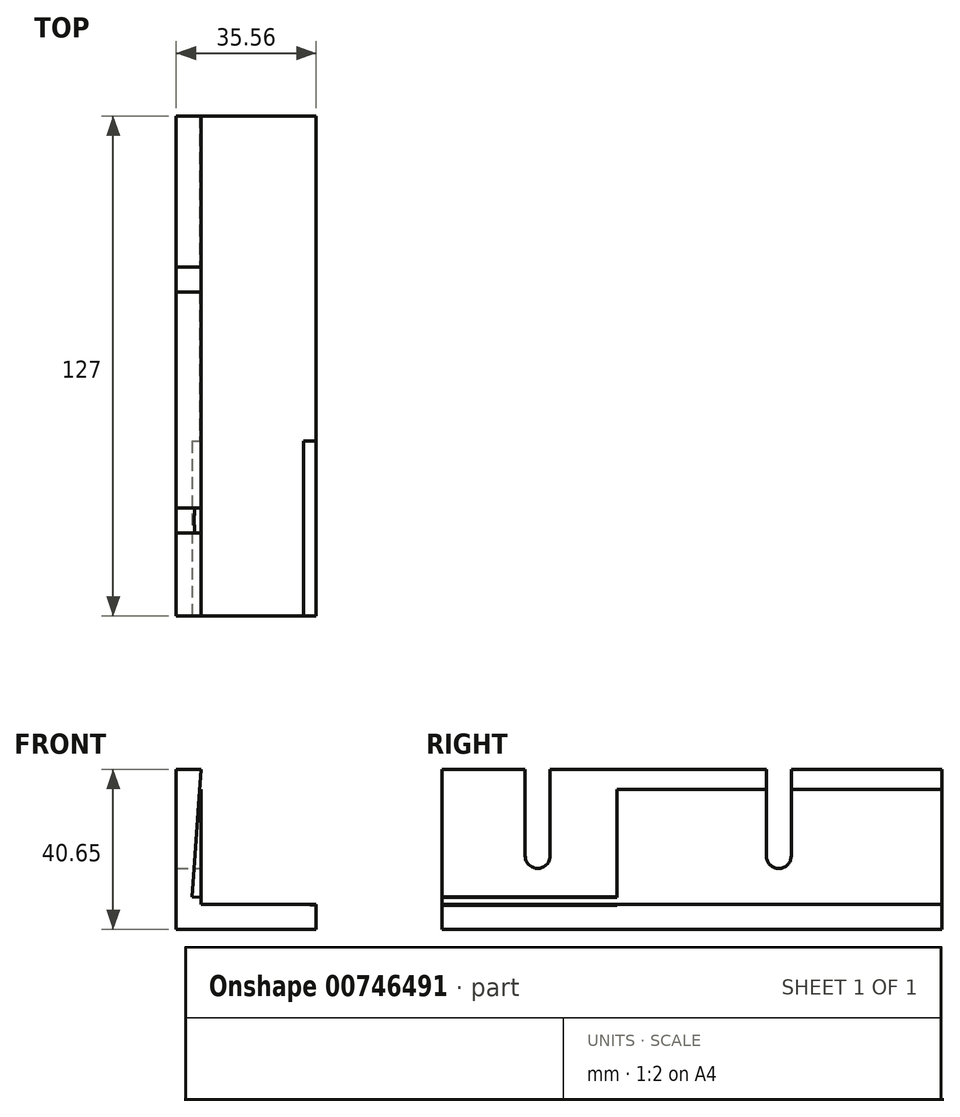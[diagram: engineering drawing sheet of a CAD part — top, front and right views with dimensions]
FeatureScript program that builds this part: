
annotation { "Feature Type Name" : "Feature", "Feature Type Description" : "" }
export const myFeature = defineFeature(function(context is Context, id is Id, definition is map)
    precondition{}
    {
        {
            var Q0;
            Q0=qCreatedBy(makeId("Front.planeOp"),FACE);
            var sketch = newSketch(context, id + "F0", { "sketchPlane" : qUnion([Q0])});
            skLineSegment(sketch, "E0", {"start": v(-33.64, 24.98) * mm, "end": v(-33.64, -39.73) * mm});
            skLineSegment(sketch, "E1", {"start": v(-33.64, -39.73) * mm, "end": v(31.06, -39.73) * mm});
            skLineSegment(sketch, "E2", {"start": v(31.06, -39.73) * mm, "end": v(31.06, 24.98) * mm});
            skLineSegment(sketch, "E3", {"start": v(-33.64, 24.98) * mm, "end": v(31.06, 24.98) * mm});
            skSolve(sketch);
        }
        {
            var Q0;
            Q0=makeQuery(id+"F0.imprint","IMPRINT",FACE,{"disambiguationData":[TD([[makeQuery(id+"F0.imprint","IMPRINT",EDGE,{"derivedFrom":sQuery(id+"F0.wireOp",EDGE,"E0")}),1.0]])]});
            extrude(context, id + "F1", {"entities" : qUnion([Q0]), "oppositeDirection" : true, "depth" : 127 * mm, "offsetDistance" : 25.4 * mm});
        }
        {
            var Q0;
            Q0=makeQuery(id+"F1.opExtrude","CAP_FACE",FACE,{"disambiguationData":[OSD([sQuery(id+"F0.wireOp",EDGE,"E0"),sQuery(id+"F0.wireOp",EDGE,"E1"),sQuery(id+"F0.wireOp",EDGE,"E2"),sQuery(id+"F0.wireOp",EDGE,"E3")])],"isStart":false});
            var sketch = newSketch(context, id + "F2", { "sketchPlane" : qUnion([Q0])});
            skLineSegment(sketch, "E4", {"start": v(33.64, -39.73) * mm, "end": v(33.64, -33.38) * mm});
            skLineSegment(sketch, "E5", {"start": v(33.64, -33.38) * mm, "end": v(27.3, -33.38) * mm});
            skLineSegment(sketch, "E6", {"start": v(27.3, -33.38) * mm, "end": v(27.3, -39.73) * mm});
            skLineSegment(sketch, "E7", {"start": v(27.3, -33.38) * mm, "end": v(-31.06, -33.38) * mm});
            skLineSegment(sketch, "E8", {"start": v(27.3, -33.38) * mm, "end": v(27.3, 24.98) * mm});
            skSolve(sketch);
        }
        {
            var Q0;
            {var subQ0=sQuery(id+"F2.wireOp",EDGE,"E7");Q0=makeQuery(id+"F2.imprint","IMPRINT",FACE,{"disambiguationData":[TD([[makeQuery(id+"F2.imprint","IMPRINT",EDGE,{"derivedFrom":subQ0}),-1.0]])]});}
            extrude(context, id + "F3", {"entities" : qUnion([Q0]), "operationType" : NewBodyOperationType.REMOVE, "endBound" : BoundingType.THROUGH_ALL, "oppositeDirection" : true, "depth" : 55.76 * mm, "offsetDistance" : 25.4 * mm});
        }
        {
            var Q0;
            Q0=makeQuery(id+"F1.opExtrude","CAP_FACE",FACE,{"disambiguationData":[OSD([sQuery(id+"F0.wireOp",EDGE,"E0"),sQuery(id+"F0.wireOp",EDGE,"E1"),sQuery(id+"F0.wireOp",EDGE,"E2"),sQuery(id+"F0.wireOp",EDGE,"E3")])],"isStart":true});
            var sketch = newSketch(context, id + "F4", { "sketchPlane" : qUnion([Q0])});
            skLineSegment(sketch, "E9", {"start": v(-27.3, 24.98) * mm, "end": v(-33.64, 24.98) * mm});
            skLineSegment(sketch, "E10", {"start": v(-33.64, 24.98) * mm, "end": v(-33.64, -39.73) * mm});
            skLineSegment(sketch, "E11", {"start": v(-33.64, -39.73) * mm, "end": v(31.06, -39.73) * mm});
            skPoint(sketch, "E12.endSnap0", {"position": v(31.06, -36.55) * mm});
            skLineSegment(sketch, "E13", {"start": v(-29.55, -31.4) * mm, "end": v(53, -37.17) * mm});
            skLineSegment(sketch, "E14", {"start": v(-29.55, -31.4) * mm, "end": v(-25.06, 32.88) * mm});
            skLineSegment(sketch, "E15", {"start": v(53, -37.17) * mm, "end": v(53, -39.73) * mm});
            skLineSegment(sketch, "E16", {"start": v(53, -39.73) * mm, "end": v(-33.64, -39.73) * mm});
            skLineSegment(sketch, "E17", {"start": v(-33.64, 32.88) * mm, "end": v(-25.06, 32.88) * mm});
            skLineSegment(sketch, "E18", {"start": v(-33.64, 32.88) * mm, "end": v(-33.64, -39.73) * mm});
            skSolve(sketch);
        }
        {
            var Q0;
            {var subQ0=sQuery(id+"F4.wireOp",EDGE,"E14");var subQ1=sQuery(id+"F4.wireOp",EDGE,"E13");var subQ2=makeQuery(id+"F4.imprint","INTERSECT",VERTEX,{"derivedFrom":[subQ1,subQ0]});Q0=makeQuery(id+"F4.imprint","IMPRINT",FACE,{"disambiguationData":[TD([[makeQuery(id+"F4.imprint","IMPRINT",EDGE,{"disambiguationData":[TD([[subQ2,-1.0]])],"derivedFrom":subQ1}),1.0]])]});}
            var Q1;
            {var subQ0=sQuery(id+"F4.wireOp",EDGE,"E13");var subQ1=sQuery(id+"F0.wireOp",EDGE,"E2");var subQ4=makeQuery(id+"F1.opExtrude","CAP_EDGE",EDGE,{"disambiguationData":[OSD([subQ1])],"isStart":true});var subQ5=makeQuery(id+"F4.imprint","INTERSECT",VERTEX,{"derivedFrom":[subQ4,subQ0]});Q1=makeQuery(id+"F4.imprint","IMPRINT",FACE,{"disambiguationData":[TD([[makeQuery(id+"F4.imprint","IMPRINT",EDGE,{"disambiguationData":[TD([[subQ5,1.0]])],"derivedFrom":subQ0}),1.0]])]});}
            extrude(context, id + "F5", {"entities" : qUnion([Q0, Q1]), "operationType" : NewBodyOperationType.REMOVE, "oppositeDirection" : true, "depth" : 44.45 * mm, "offsetDistance" : 25.4 * mm});
        }
        {
            var Q0;
            Q0=makeQuery(id+"F3.boolean.opBoolean","COPY",FACE,{"derivedFrom":makeQuery(id+"F3.opExtrude","SWEPT_FACE",FACE,{"disambiguationData":[OSD([sQuery(id+"F2.wireOp",EDGE,"E8")])]})});
            var sketch = newSketch(context, id + "F6", { "sketchPlane" : qUnion([Q0])});
            skLineSegment(sketch, "E19", {"start": v(27.44, 24.98) * mm, "end": v(127, 24.98) * mm});
            skLineSegment(sketch, "E20", {"start": v(127, 24.98) * mm, "end": v(127, -33.38) * mm});
            skLineSegment(sketch, "E21", {"start": v(127, -33.38) * mm, "end": v(0, -33.38) * mm});
            skLineSegment(sketch, "E22", {"start": v(0, -33.38) * mm, "end": v(0, 24.98) * mm});
            skLineSegment(sketch, "E23", {"start": v(0, 24.98) * mm, "end": v(21.09, 24.98) * mm});
            skArc(sketch, "E24", {"start": v(82.35, -21.06) * mm, "mid": v(85.53, -24.23) * mm, "end": v(88.7, -21.06) * mm});
            skLineSegment(sketch, "E25", {"start": v(88.7, -21.06) * mm, "end": v(88.7, 24.98) * mm});
            skLineSegment(sketch, "E26", {"start": v(82.35, -21.06) * mm, "end": v(82.35, 24.98) * mm});
            skArc(sketch, "E27", {"start": v(21.09, -21.06) * mm, "mid": v(24.26, -24.23) * mm, "end": v(27.44, -21.06) * mm});
            skLineSegment(sketch, "E28", {"start": v(21.09, -21.06) * mm, "end": v(21.09, 24.98) * mm});
            skLineSegment(sketch, "E29", {"start": v(27.44, -21.06) * mm, "end": v(27.44, 24.98) * mm});
            skLineSegment(sketch, "E30", {"start": v(27.44, 24.98) * mm, "end": v(21.09, 24.98) * mm});
            skPoint(sketch, "E31.endSnap0", {"position": v(24.26, -24.23) * mm});
            skSolve(sketch);
        }
        {
            var Q0;
            {var subQ1=sQuery(id+"F6.wireOp",EDGE,"c31WWHYK-vBc0-QJFG-3EGz-c6wR2XxRCZ5n");var subQ4=sQuery(id+"F6.wireOp",EDGE,"BnuWwshu-QowS-UM11-6egq-2gLvmHulIOIC");var subQ5=makeQuery(id+"F6.imprint","INTERSECT",VERTEX,{"derivedFrom":[subQ1,subQ4]});Q0=makeQuery(id+"F6.imprint","IMPRINT",FACE,{"disambiguationData":[TD([[makeQuery(id+"F6.imprint","IMPRINT",EDGE,{"disambiguationData":[TD([[subQ5,-1.0]])],"derivedFrom":subQ1}),1.0]])]});}
            var Q1;
            {var subQ0=sQuery(id+"F6.wireOp",EDGE,"PxgFI6bS-cj6o-HxTh-fpXl-rELYx5VuJGPC");var subQ9=sQuery(id+"F6.wireOp",EDGE,"BnuWwshu-QowS-UM11-6egq-2gLvmHulIOIC");var subQ10=makeQuery(id+"F6.imprint","INTERSECT",VERTEX,{"derivedFrom":[subQ0,subQ9]});Q1=makeQuery(id+"F6.imprint","IMPRINT",FACE,{"disambiguationData":[TD([[makeQuery(id+"F6.imprint","IMPRINT",EDGE,{"disambiguationData":[TD([[subQ10,-1.0]])],"derivedFrom":subQ0}),-1.0]])]});}
            var Q2;
            Q2=makeQuery(id+"F6.imprint","IMPRINT",FACE,{"disambiguationData":[TD([[makeQuery(id+"F6.imprint","IMPRINT",EDGE,{"derivedFrom":sQuery(id+"F6.wireOp",EDGE,"nVCfulUX-UBZk-rReu-1cFz-JZFjZ0D3dsWO")}),1.0]])]});
            var Q3;
            {var subQ0=sQuery(id+"F6.wireOp",EDGE,"BnuWwshu-QowS-UM11-6egq-2gLvmHulIOIC");var subQ1=sQuery(id+"F2.wireOp",EDGE,"E8");var subQ2=sQuery(id+"F0.wireOp",EDGE,"E3");var subQ3=makeQuery(id+"F3.boolean.opBoolean","COPY",EDGE,{"derivedFrom":makeQuery(id+"F3.opExtrude","SWEPT_EDGE",EDGE,{"disambiguationData":[OSD([subQ2,subQ1])]})});var subQ4=makeQuery(id+"F6.imprint","INTERSECT",VERTEX,{"derivedFrom":[subQ3,subQ0]});Q3=makeQuery(id+"F6.imprint","IMPRINT",FACE,{"disambiguationData":[TD([[makeQuery(id+"F6.imprint","IMPRINT",EDGE,{"disambiguationData":[TD([[subQ4,-1.0]])],"derivedFrom":subQ3}),-1.0]])]});}
            var Q4;
            {var subQ0=sQuery(id+"F6.wireOp",EDGE,"E23");var subQ1=sQuery(id+"F6.wireOp",EDGE,"GWAlOemz-n7tp-SVu9-tSwS-dO0S4uVOhK2H");var subQ2=makeQuery(id+"F6.imprint","INTERSECT",VERTEX,{"derivedFrom":[subQ1,subQ0]});Q4=makeQuery(id+"F6.imprint","IMPRINT",FACE,{"disambiguationData":[TD([[makeQuery(id+"F6.imprint","IMPRINT",EDGE,{"disambiguationData":[TD([[subQ2,-1.0]])],"derivedFrom":subQ0}),-1.0]])]});}
            var Q5;
            {var subQ0=sQuery(id+"F6.wireOp",EDGE,"YNUtTdzb-W802-iu6F-8lba-iVoMnU8XWFkd");Q5=makeQuery(id+"F6.imprint","IMPRINT",FACE,{"disambiguationData":[TD([[makeQuery(id+"F6.imprint","IMPRINT",EDGE,{"derivedFrom":subQ0}),1.0]])]});}
            var Q6;
            Q6=makeQuery(id+"F6.imprint","IMPRINT",FACE,{"disambiguationData":[TD([[makeQuery(id+"F6.imprint","IMPRINT",EDGE,{"derivedFrom":sQuery(id+"F6.wireOp",EDGE,"f8IW44Pr-O293-7rfo-ai8i-kcAhvm2oJwU2")}),1.0]])]});
            var Q7;
            {var subQ0=sQuery(id+"F6.wireOp",EDGE,"E30");Q7=makeQuery(id+"F6.imprint","IMPRINT",FACE,{"disambiguationData":[TD([[makeQuery(id+"F6.imprint","IMPRINT",EDGE,{"derivedFrom":subQ0}),-1.0]])]});}
            var Q8;
            {var subQ0=sQuery(id+"F6.wireOp",EDGE,"E27");Q8=makeQuery(id+"F6.imprint","IMPRINT",FACE,{"disambiguationData":[TD([[makeQuery(id+"F6.imprint","IMPRINT",EDGE,{"derivedFrom":subQ0}),1.0]])]});}
            var Q9;
            Q9=makeQuery(id+"F6.imprint","IMPRINT",FACE,{"disambiguationData":[TD([[makeQuery(id+"F6.imprint","IMPRINT",EDGE,{"derivedFrom":sQuery(id+"F6.wireOp",EDGE,"E24")}),1.0]])]});
            extrude(context, id + "F7", {"entities" : qUnion([Q0, Q1, Q2, Q3, Q4, Q5, Q6, Q7, Q8, Q9]), "operationType" : NewBodyOperationType.REMOVE, "endBound" : BoundingType.THROUGH_ALL, "oppositeDirection" : true, "depth" : 25.4 * mm, "offsetDistance" : 25.4 * mm});
        }
        {
            var Q0;
            Q0=makeQuery(id+"F1.opExtrude","CAP_FACE",FACE,{"disambiguationData":[OSD([sQuery(id+"F0.wireOp",EDGE,"E0"),sQuery(id+"F0.wireOp",EDGE,"E1"),sQuery(id+"F0.wireOp",EDGE,"E2"),sQuery(id+"F0.wireOp",EDGE,"E3")])],"isStart":true});
            var sketch = newSketch(context, id + "F8", { "sketchPlane" : qUnion([Q0])});
            skPoint(sketch, "E32.end.orphan", {"position": v(31.06, -11.79) * mm});
            skLineSegment(sketch, "E33", {"start": v(-33.64, -39.73) * mm, "end": v(1.92, -39.73) * mm});
            skLineSegment(sketch, "E34", {"start": v(-33.64, -39.73) * mm, "end": v(-33.64, -4.17) * mm});
            skLineSegment(sketch, "E35", {"start": v(-33.64, -4.17) * mm, "end": v(1.92, -4.17) * mm});
            skLineSegment(sketch, "E36", {"start": v(1.92, -4.17) * mm, "end": v(1.92, -39.73) * mm});
            skLineSegment(sketch, "E37", {"start": v(1.92, -4.17) * mm, "end": v(1.92, 31.35) * mm});
            skLineSegment(sketch, "E38", {"start": v(1.92, 31.35) * mm, "end": v(-33.64, 31.35) * mm});
            skLineSegment(sketch, "E39", {"start": v(-33.64, 31.35) * mm, "end": v(-33.64, -4.17) * mm});
            skLineSegment(sketch, "E40", {"start": v(1.92, 31.35) * mm, "end": v(31.06, 31.35) * mm});
            skLineSegment(sketch, "E41", {"start": v(31.06, 31.35) * mm, "end": v(31.06, -39.73) * mm});
            skLineSegment(sketch, "E42", {"start": v(31.06, -39.73) * mm, "end": v(1.92, -39.73) * mm});
            skSolve(sketch);
        }
        {
            var Q0;
            {var subQ1=sQuery(id+"F8.wireOp",EDGE,"iYOc6YzF-aGtb-jNaQ-08vX-AgNLz6LKXQLZ");Q0=makeQuery(id+"F8.imprint","IMPRINT",FACE,{"disambiguationData":[TD([[makeQuery(id+"F8.imprint","IMPRINT",EDGE,{"derivedFrom":subQ1}),1.0]])]});}
            var Q1;
            {var subQ5=sQuery(id+"F8.wireOp",EDGE,"VOdGziPm-6em2-h7AQ-acnH-AUfeopXnjPFy");Q1=makeQuery(id+"F8.imprint","IMPRINT",FACE,{"disambiguationData":[TD([[makeQuery(id+"F8.imprint","IMPRINT",EDGE,{"derivedFrom":subQ5}),-1.0]])]});}
            var Q2;
            {var subQ11=sQuery(id+"F8.wireOp",EDGE,"E37");Q2=makeQuery(id+"F8.imprint","IMPRINT",FACE,{"disambiguationData":[TD([[makeQuery(id+"F8.imprint","IMPRINT",EDGE,{"derivedFrom":subQ11}),1.0]])]});}
            var Q3;
            {var subQ0=sQuery(id+"F0.wireOp",EDGE,"E3");var subQ1=makeQuery(id+"F1.opExtrude","CAP_EDGE",EDGE,{"disambiguationData":[OSD([subQ0])],"isStart":true});Q3=makeQuery(id+"F8.imprint","IMPRINT",FACE,{"disambiguationData":[TD([[makeQuery(id+"F8.imprint","IMPRINT",EDGE,{"derivedFrom":subQ1}),-1.0]])]});}
            var Q4;
            {var subQ4=sQuery(id+"F8.wireOp",EDGE,"E42");Q4=makeQuery(id+"F8.imprint","IMPRINT",FACE,{"disambiguationData":[TD([[makeQuery(id+"F8.imprint","IMPRINT",EDGE,{"derivedFrom":subQ4}),1.0]])]});}
            var Q5;
            {var subQ9=sQuery(id+"F8.wireOp",EDGE,"E37");Q5=makeQuery(id+"F8.imprint","IMPRINT",FACE,{"disambiguationData":[TD([[makeQuery(id+"F8.imprint","IMPRINT",EDGE,{"derivedFrom":subQ9}),-1.0]])]});}
            extrude(context, id + "F9", {"entities" : qUnion([Q0, Q1, Q2, Q3, Q4, Q5]), "operationType" : NewBodyOperationType.REMOVE, "endBound" : BoundingType.THROUGH_ALL, "oppositeDirection" : true, "depth" : 25.4 * mm, "offsetDistance" : 25.4 * mm});
        }
    });
